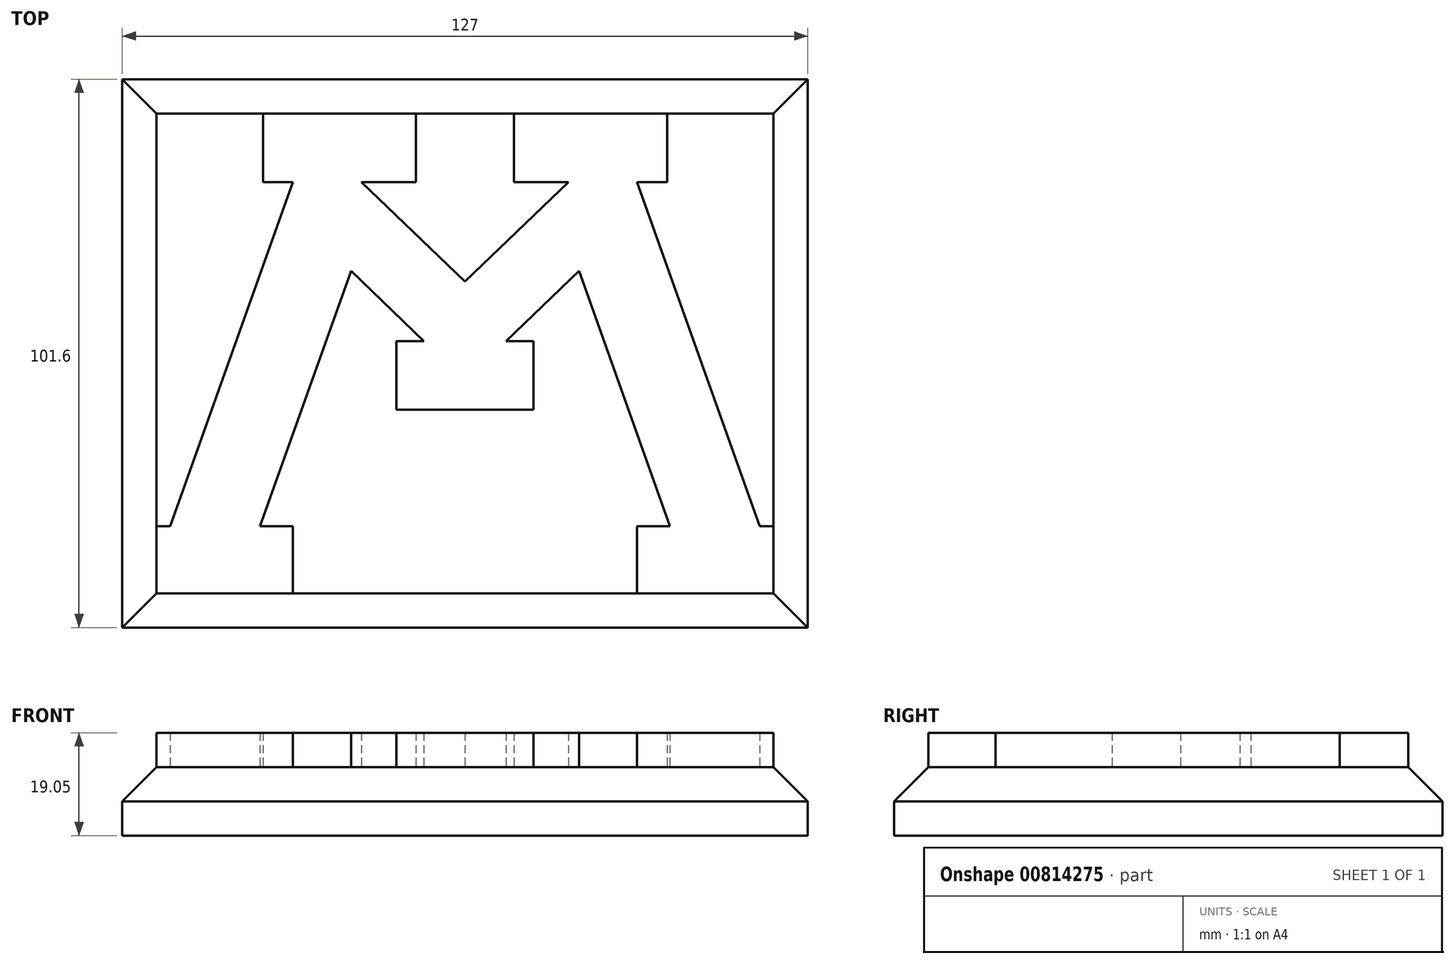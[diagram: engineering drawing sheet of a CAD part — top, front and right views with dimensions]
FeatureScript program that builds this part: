
annotation { "Feature Type Name" : "Feature", "Feature Type Description" : "" }
export const myFeature = defineFeature(function(context is Context, id is Id, definition is map)
    precondition{}
    {
        {
            var Q0;
            Q0=qCreatedBy(makeId("Top.planeOp"),FACE);
            var sketch = newSketch(context, id + "F0", { "sketchPlane" : qUnion([Q0])});
            skLineSegment(sketch, "E0.bottom", {"start": v(0, 0) * mm, "end": v(127, 0) * mm});
            skLineSegment(sketch, "E0.top", {"start": v(0, 101.6) * mm, "end": v(127, 101.6) * mm});
            skLineSegment(sketch, "E0.left", {"start": v(0, 0) * mm, "end": v(0, 101.6) * mm});
            skLineSegment(sketch, "E0.right", {"start": v(127, 0) * mm, "end": v(127, 101.6) * mm});
            skSolve(sketch);
        }
        {
            var Q0;
            Q0=makeQuery(id+"F0.imprint","IMPRINT",FACE,{"disambiguationData":[TD([[makeQuery(id+"F0.imprint","IMPRINT",EDGE,{"derivedFrom":sQuery(id+"F0.wireOp",EDGE,"E0.bottom")}),1.0]])]});
            extrude(context, id + "F1", {"entities" : qUnion([Q0]), "depth" : 12.7 * mm, "offsetDistance" : 25.4 * mm});
        }
        {
            var Q0;
            Q0=makeQuery(id+"F1.opExtrude","CAP_EDGE",EDGE,{"disambiguationData":[OSD([sQuery(id+"F0.wireOp",EDGE,"E0.left")])],"isStart":false});
            var Q1;
            Q1=makeQuery(id+"F1.opExtrude","CAP_EDGE",EDGE,{"disambiguationData":[OSD([sQuery(id+"F0.wireOp",EDGE,"E0.top")])],"isStart":false});
            var Q2;
            Q2=makeQuery(id+"F1.opExtrude","CAP_EDGE",EDGE,{"disambiguationData":[OSD([sQuery(id+"F0.wireOp",EDGE,"E0.right")])],"isStart":false});
            var Q3;
            Q3=makeQuery(id+"F1.opExtrude","CAP_EDGE",EDGE,{"disambiguationData":[OSD([sQuery(id+"F0.wireOp",EDGE,"E0.bottom")])],"isStart":false});
            chamfer(context, id + "F2", {"entities" : qUnion([Q0, Q1, Q2, Q3]), "width" : 6.35 * mm, "tangentPropagation" : true});
        }
        {
            var Q0;
            Q0=makeQuery(id+"F1.opExtrude","CAP_FACE",FACE,{"disambiguationData":[OSD([sQuery(id+"F0.wireOp",EDGE,"E0.bottom"),sQuery(id+"F0.wireOp",EDGE,"E0.top"),sQuery(id+"F0.wireOp",EDGE,"E0.left"),sQuery(id+"F0.wireOp",EDGE,"E0.right")])],"isStart":false});
            var sketch = newSketch(context, id + "F3", { "sketchPlane" : qUnion([Q0])});
            skLineSegment(sketch, "E1", {"start": v(63.5, 95.25) * mm, "end": v(63.5, 6.35) * mm, "construction": true});
            skLineSegment(sketch, "E2", {"start": v(63.5, 64.08) * mm, "end": v(44.33, 82.55) * mm});
            skLineSegment(sketch, "E3", {"start": v(44.33, 82.55) * mm, "end": v(54.42, 82.55) * mm});
            skLineSegment(sketch, "E4", {"start": v(54.42, 82.55) * mm, "end": v(54.42, 95.25) * mm});
            skLineSegment(sketch, "E5", {"start": v(54.42, 95.25) * mm, "end": v(26.08, 95.25) * mm});
            skLineSegment(sketch, "E6", {"start": v(26.08, 95.25) * mm, "end": v(26.08, 82.55) * mm});
            skLineSegment(sketch, "E7", {"start": v(26.08, 82.55) * mm, "end": v(31.63, 82.55) * mm});
            skLineSegment(sketch, "E8", {"start": v(31.63, 82.55) * mm, "end": v(8.9, 18.8) * mm});
            skLineSegment(sketch, "E9", {"start": v(8.9, 18.8) * mm, "end": v(6.35, 18.8) * mm});
            skLineSegment(sketch, "E10", {"start": v(6.35, 18.8) * mm, "end": v(6.35, 6.35) * mm});
            skLineSegment(sketch, "E11", {"start": v(6.35, 6.35) * mm, "end": v(31.63, 6.35) * mm});
            skLineSegment(sketch, "E12", {"start": v(31.63, 6.35) * mm, "end": v(31.63, 18.8) * mm});
            skLineSegment(sketch, "E13", {"start": v(31.63, 18.8) * mm, "end": v(25.54, 18.8) * mm});
            skLineSegment(sketch, "E14", {"start": v(25.54, 18.8) * mm, "end": v(42.39, 66.07) * mm});
            skLineSegment(sketch, "E15.MirrorCS", {"start": v(63.5, 64.08) * mm, "end": v(82.67, 82.55) * mm});
            skLineSegment(sketch, "E16.MirrorCS", {"start": v(82.67, 82.55) * mm, "end": v(72.58, 82.55) * mm});
            skLineSegment(sketch, "E17.MirrorCS", {"start": v(72.58, 95.25) * mm, "end": v(100.92, 95.25) * mm});
            skLineSegment(sketch, "E18.MirrorCS", {"start": v(100.92, 95.25) * mm, "end": v(100.92, 82.55) * mm});
            skLineSegment(sketch, "E19.MirrorCS", {"start": v(100.92, 82.55) * mm, "end": v(95.37, 82.55) * mm});
            skLineSegment(sketch, "E20.MirrorCS", {"start": v(95.37, 82.55) * mm, "end": v(118.1, 18.8) * mm});
            skLineSegment(sketch, "E21.MirrorCS", {"start": v(101.46, 18.8) * mm, "end": v(84.61, 66.07) * mm});
            skLineSegment(sketch, "E22.MirrorCS", {"start": v(118.1, 18.8) * mm, "end": v(120.65, 18.8) * mm});
            skLineSegment(sketch, "E23.MirrorCS", {"start": v(120.65, 18.8) * mm, "end": v(120.65, 6.35) * mm});
            skLineSegment(sketch, "E24.MirrorCS", {"start": v(120.65, 6.35) * mm, "end": v(95.37, 6.35) * mm});
            skLineSegment(sketch, "E25.MirrorCS", {"start": v(95.37, 6.35) * mm, "end": v(95.37, 18.8) * mm});
            skLineSegment(sketch, "E26.MirrorCS", {"start": v(95.37, 18.8) * mm, "end": v(101.46, 18.8) * mm});
            skLineSegment(sketch, "E27.MirrorCS", {"start": v(72.58, 82.55) * mm, "end": v(72.58, 95.25) * mm});
            skLineSegment(sketch, "E28", {"start": v(42.39, 66.07) * mm, "end": v(55.88, 53.07) * mm});
            skLineSegment(sketch, "E29", {"start": v(55.88, 53.07) * mm, "end": v(50.8, 53.07) * mm});
            skLineSegment(sketch, "E30", {"start": v(50.8, 53.07) * mm, "end": v(50.8, 40.37) * mm});
            skLineSegment(sketch, "E31", {"start": v(50.8, 40.37) * mm, "end": v(76.2, 40.37) * mm});
            skLineSegment(sketch, "E32", {"start": v(76.2, 40.37) * mm, "end": v(76.2, 53.07) * mm});
            skLineSegment(sketch, "E33", {"start": v(76.2, 53.07) * mm, "end": v(71.12, 53.07) * mm});
            skLineSegment(sketch, "E34", {"start": v(71.12, 53.07) * mm, "end": v(84.61, 66.07) * mm});
            skSolve(sketch);
        }
        {
            var Q0;
            Q0 = qSketchRegion(id + "F3", true);
            extrude(context, id + "F4", {"entities" : qUnion([Q0]), "operationType" : NewBodyOperationType.ADD, "depth" : 6.35 * mm, "offsetDistance" : 25.4 * mm});
        }
    });
